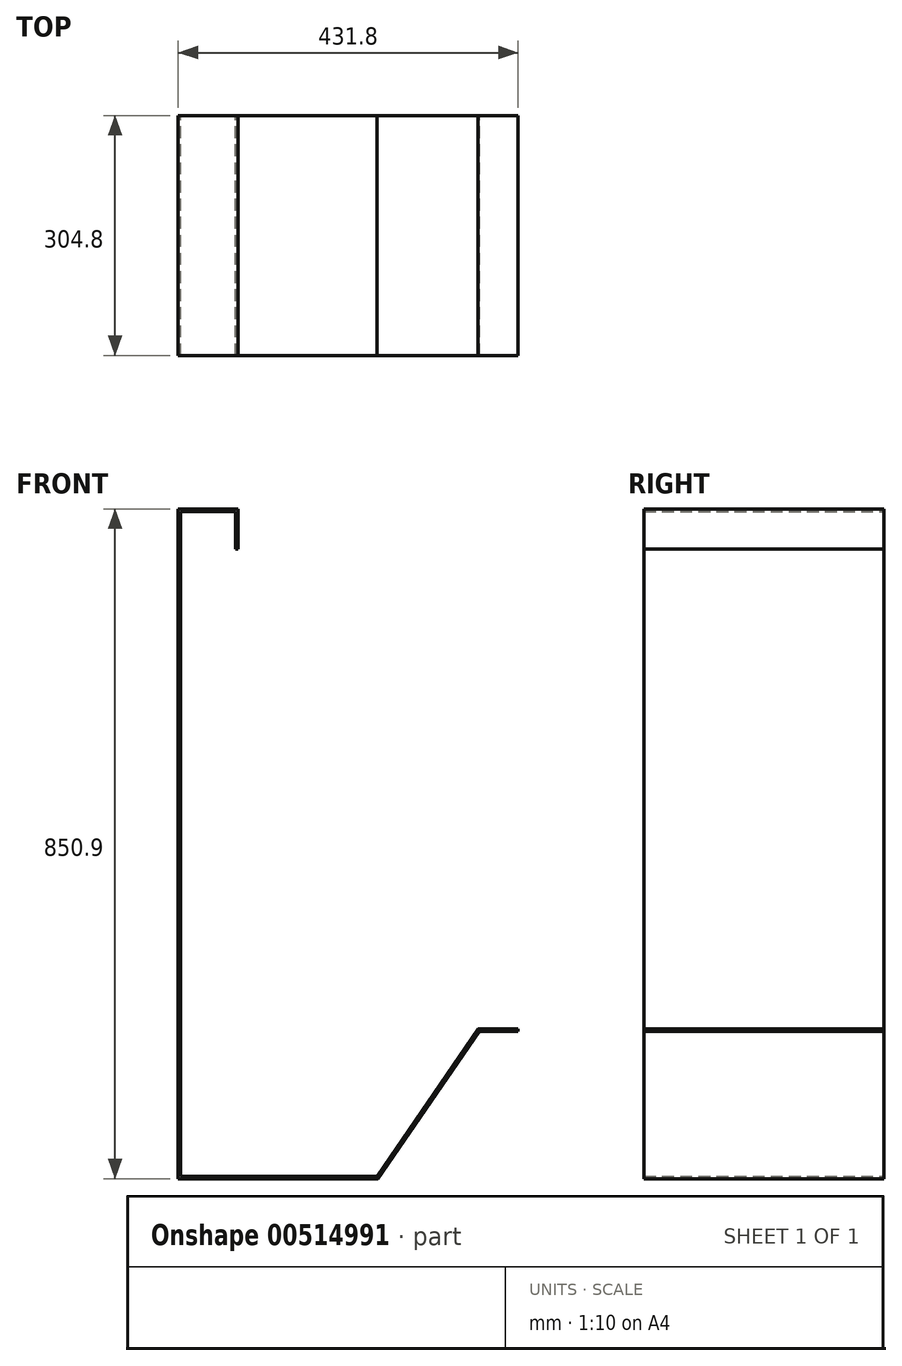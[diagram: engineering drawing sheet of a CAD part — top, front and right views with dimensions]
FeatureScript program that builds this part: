
annotation { "Feature Type Name" : "Feature", "Feature Type Description" : "" }
export const myFeature = defineFeature(function(context is Context, id is Id, definition is map)
    precondition{}
    {
        {
            var Q0;
            Q0=qCreatedBy(makeId("Front.planeOp"),FACE);
            var sketch = newSketch(context, id + "F0", { "sketchPlane" : qUnion([Q0])});
            skLineSegment(sketch, "E0", {"start": v(0, 0) * mm, "end": v(0, 850.9) * mm});
            skLineSegment(sketch, "E1", {"start": v(0, 850.9) * mm, "end": v(76.2, 850.9) * mm});
            skLineSegment(sketch, "E2", {"start": v(0, 0) * mm, "end": v(254, 0) * mm});
            skLineSegment(sketch, "E3", {"start": v(254, 0) * mm, "end": v(382.67, 187.32) * mm});
            skLineSegment(sketch, "E4", {"start": v(76.2, 850.9) * mm, "end": v(76.2, 800.1) * mm});
            skLineSegment(sketch, "E5.0", {"start": v(73.03, 847.73) * mm, "end": v(73.03, 800.1) * mm});
            skLineSegment(sketch, "E5.1", {"start": v(252.33, 3.17) * mm, "end": v(381, 190.5) * mm});
            skLineSegment(sketch, "E5.2", {"start": v(3.17, 3.17) * mm, "end": v(252.33, 3.17) * mm});
            skLineSegment(sketch, "E5.3", {"start": v(3.17, 3.17) * mm, "end": v(3.17, 847.73) * mm});
            skLineSegment(sketch, "E5.4", {"start": v(3.17, 847.73) * mm, "end": v(73.03, 847.73) * mm});
            skLineSegment(sketch, "E6", {"start": v(73.03, 800.1) * mm, "end": v(76.2, 800.1) * mm});
            skLineSegment(sketch, "E7", {"start": v(381, 190.5) * mm, "end": v(431.8, 190.5) * mm});
            skLineSegment(sketch, "E8.0", {"start": v(382.67, 187.32) * mm, "end": v(431.8, 187.32) * mm});
            skLineSegment(sketch, "E9", {"start": v(431.8, 187.32) * mm, "end": v(431.8, 190.5) * mm});
            skSolve(sketch);
        }
        {
            var Q0;
            Q0=makeQuery(id+"F0.imprint","IMPRINT",FACE,{"disambiguationData":[TD([[makeQuery(id+"F0.imprint","IMPRINT",EDGE,{"derivedFrom":sQuery(id+"F0.wireOp",EDGE,"E0")}),-1.0]])]});
            extrude(context, id + "F1", {"entities" : qUnion([Q0]), "depth" : 304.8 * mm, "offsetDistance" : 25.4 * mm});
        }
    });
